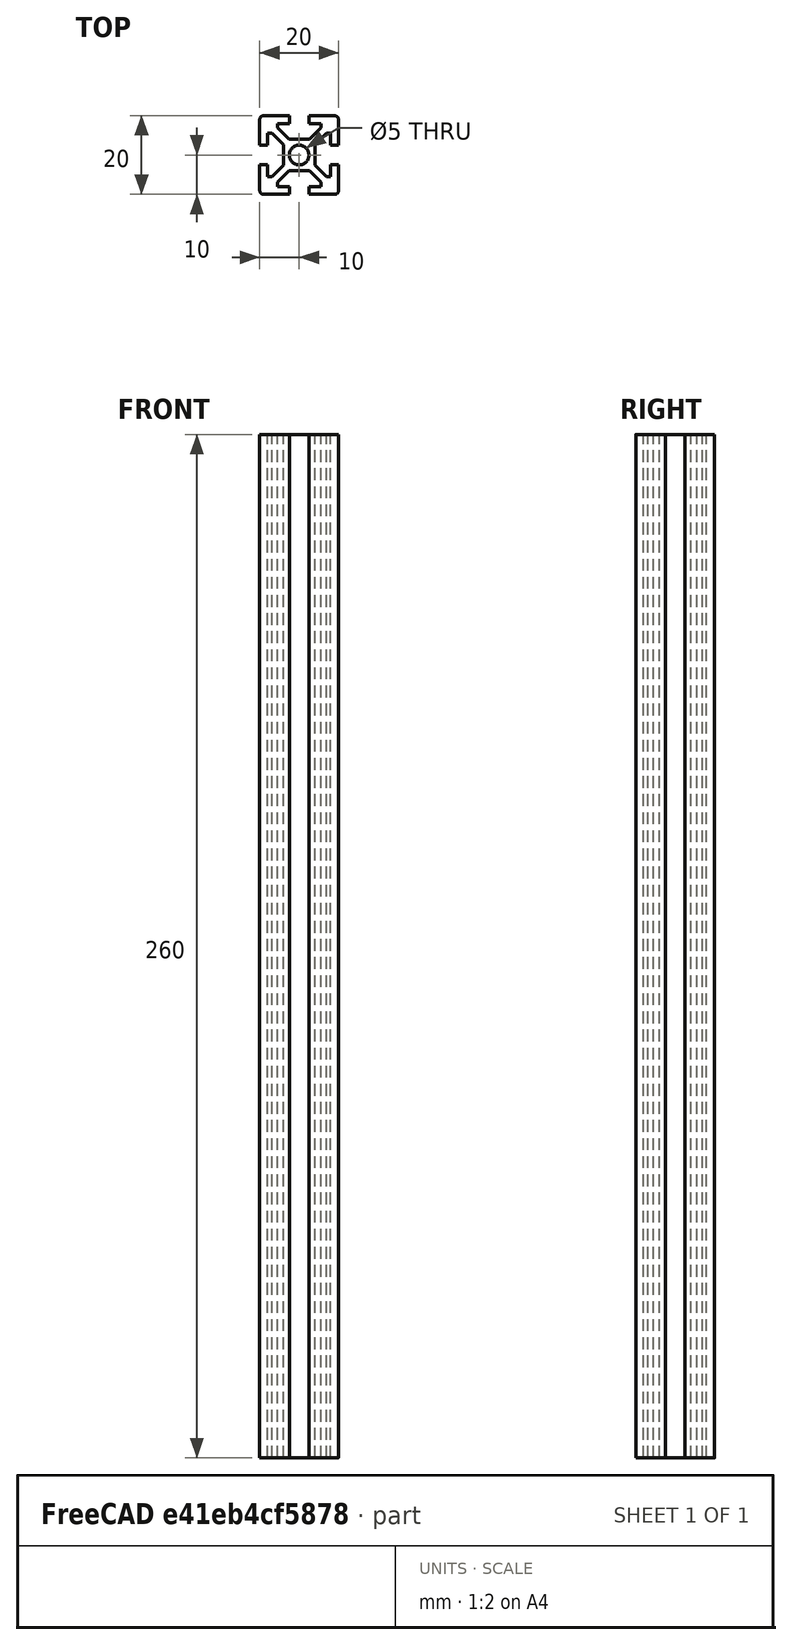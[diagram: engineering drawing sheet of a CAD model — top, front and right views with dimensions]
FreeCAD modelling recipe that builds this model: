
FCSTD DOCUMENT  (FreeCAD 0.18R16117 (Git))
Label: profile2020
License: All rights reserved
LicenseURL: http://en.wikipedia.org/wiki/All_rights_reserved
objects: Sketcher::SketchObject×1, PartDesign::Pad×1, PartDesign::Body×1
note: 4 computed .brp shape members not serialized (recipe doc carries the construction recipe); baked Part::Feature solids carry a one-line shape summary decoded from their .brp

FEATURE [Sketcher::SketchObject] Sketch005  label="profile2020Sketch"
  MapMode = 5
  sketch-geometry (49):
    g0: LineSegment StartX=-4 StartY=-2.58579 StartZ=0 EndX=-4 EndY=2.58579 EndZ=0
    g1: LineSegment StartX=2.58579 StartY=4 StartZ=0 EndX=-2.58579 EndY=4 EndZ=0
    g2: LineSegment StartX=-4 StartY=2.58579 StartZ=0 EndX=-6.91421 EndY=5.5 EndZ=0
    g3: LineSegment StartX=-2.58579 StartY=4 StartZ=0 EndX=-5.5 EndY=6.91421 EndZ=0
    g4: LineSegment StartX=-6.91421 StartY=5.5 StartZ=0 EndX=-8 EndY=5.5 EndZ=0
    g5: LineSegment StartX=-8 StartY=5.5 StartZ=0 EndX=-8 EndY=2.5 EndZ=0
    g6: LineSegment StartX=-5.5 StartY=6.91421 StartZ=0 EndX=-5.5 EndY=8 EndZ=0
    g7: LineSegment StartX=-5.5 StartY=8 StartZ=0 EndX=-2.5 EndY=8 EndZ=0
    g8: LineSegment StartX=-8 StartY=2.5 StartZ=0 EndX=-10 EndY=2.5 EndZ=0
    g9: LineSegment StartX=-2.5 StartY=8 StartZ=0 EndX=-2.5 EndY=10 EndZ=0
    g10: LineSegment StartX=-2.5 StartY=10 StartZ=0 EndX=-9 EndY=10 EndZ=0
    g11: LineSegment StartX=-10 StartY=2.5 StartZ=0 EndX=-10 EndY=9 EndZ=0
    g12: ArcOfCircle CenterX=-9 CenterY=9 CenterZ=0 NormalX=0 NormalY=0 NormalZ=1 AngleXU=0 Radius=1 StartAngle=1.5708 EndAngle=3.14159
    g13: Circle CenterX=0 CenterY=0 CenterZ=0 NormalX=0 NormalY=0 NormalZ=1 AngleXU=0 Radius=2.5
    g14: LineSegment StartX=4 StartY=2.58579 StartZ=0 EndX=4 EndY=-2.58579 EndZ=0
    g15: LineSegment StartX=2.58579 StartY=4 StartZ=0 EndX=5.5 EndY=6.91421 EndZ=0
    g16: LineSegment StartX=5.5 StartY=6.91421 StartZ=0 EndX=5.5 EndY=8 EndZ=0
    g17: LineSegment StartX=5.5 StartY=8 StartZ=0 EndX=2.5 EndY=8 EndZ=0
    g18: LineSegment StartX=2.5 StartY=8 StartZ=0 EndX=2.5 EndY=10 EndZ=0
    g19: LineSegment StartX=4 StartY=2.58579 StartZ=0 EndX=6.91421 EndY=5.5 EndZ=0
    g20: LineSegment StartX=6.91421 StartY=5.5 StartZ=0 EndX=8 EndY=5.5 EndZ=0
    g21: LineSegment StartX=8 StartY=5.5 StartZ=0 EndX=8 EndY=2.5 EndZ=0
    g22: LineSegment StartX=8 StartY=2.5 StartZ=0 EndX=10 EndY=2.5 EndZ=0
    g23: LineSegment StartX=10 StartY=2.5 StartZ=0 EndX=10 EndY=9 EndZ=0
    g24: LineSegment StartX=2.5 StartY=10 StartZ=0 EndX=9 EndY=10 EndZ=0
    g25: ArcOfCircle CenterX=9 CenterY=9 CenterZ=0 NormalX=0 NormalY=0 NormalZ=1 AngleXU=0 Radius=1 StartAngle=5.30563e-07 EndAngle=1.5708
    g26: LineSegment StartX=4 StartY=-2.58579 StartZ=0 EndX=6.91421 EndY=-5.5 EndZ=0
    g27: LineSegment StartX=6.91421 StartY=-5.5 StartZ=0 EndX=8 EndY=-5.5 EndZ=0
    g28: LineSegment StartX=8 StartY=-5.5 StartZ=0 EndX=8 EndY=-2.5 EndZ=0
    g29: LineSegment StartX=8 StartY=-2.5 StartZ=0 EndX=10 EndY=-2.5 EndZ=0
    g30: LineSegment StartX=10 StartY=-2.5 StartZ=0 EndX=10 EndY=-9 EndZ=0
    g31: LineSegment StartX=9 StartY=-10 StartZ=0 EndX=2.5 EndY=-10 EndZ=0
    g32: LineSegment StartX=2.5 StartY=-10 StartZ=0 EndX=2.5 EndY=-8 EndZ=0
    g33: LineSegment StartX=2.5 StartY=-8 StartZ=0 EndX=5.5 EndY=-8 EndZ=0
    g34: LineSegment StartX=5.5 StartY=-8 StartZ=0 EndX=5.5 EndY=-6.91421 EndZ=0
    g35: LineSegment StartX=5.5 StartY=-6.91421 StartZ=0 EndX=2.58579 EndY=-4 EndZ=0
    g36: LineSegment StartX=2.58579 StartY=-4 StartZ=0 EndX=-2.58579 EndY=-4 EndZ=0
    g37: LineSegment StartX=-2.58579 StartY=-4 StartZ=0 EndX=-5.5 EndY=-6.91421 EndZ=0
    g38: LineSegment StartX=-5.5 StartY=-6.91421 StartZ=0 EndX=-5.5 EndY=-8 EndZ=0
    g39: LineSegment StartX=-5.5 StartY=-8 StartZ=0 EndX=-2.5 EndY=-8 EndZ=0
    g40: LineSegment StartX=-2.5 StartY=-8 StartZ=0 EndX=-2.5 EndY=-10 EndZ=0
    g41: LineSegment StartX=-2.5 StartY=-10 StartZ=0 EndX=-9 EndY=-10 EndZ=0
    g42: ArcOfCircle CenterX=9 CenterY=-9 CenterZ=0 NormalX=0 NormalY=0 NormalZ=1 AngleXU=0 Radius=1 StartAngle=4.71239 EndAngle=6.28318
    g43: LineSegment StartX=-4 StartY=-2.58579 StartZ=0 EndX=-6.91421 EndY=-5.5 EndZ=0
    g44: LineSegment StartX=-6.91421 StartY=-5.5 StartZ=0 EndX=-8 EndY=-5.5 EndZ=0
    g45: LineSegment StartX=-8 StartY=-5.5 StartZ=0 EndX=-8 EndY=-2.5 EndZ=0
    g46: LineSegment StartX=-8 StartY=-2.5 StartZ=0 EndX=-10 EndY=-2.5 EndZ=0
    g47: LineSegment StartX=-10 StartY=-2.5 StartZ=0 EndX=-10 EndY=-9 EndZ=0
    g48: ArcOfCircle CenterX=-9 CenterY=-9 CenterZ=0 NormalX=0 NormalY=0 NormalZ=1 AngleXU=0 Radius=1 StartAngle=3.14159 EndAngle=4.71239
  constraints (114):
    c: DistanceX(g-1,g0) = -4
    c: Vertical(g0)
    c: Equal(g0,g1)
    c: Coincident(g0,g2)
    c: Angle(g2,g0) = 2.35619
    c: Coincident(g3,g1)
    c: Parallel(g2,g3)
    c: Equal(g3,g2)
    c: Coincident(g4,g2)
    c: Horizontal(g4)
    c: Coincident(g4,g5)
    c: Vertical(g5)
    c: Coincident(g6,g3)
    c: Vertical(g6)
    c: Equal(g4,g6)
    c: Coincident(g7,g6)
    c: Horizontal(g7)
    c: Equal(g7,g5)
    c: Coincident(g8,g5)
    c: Horizontal(g8)
    c: Coincident(g9,g7)
    c: Vertical(g9)
    c: DistanceX(g-1,g7) = -2.5
    c: DistanceY(g9) = 2
    c: Coincident(g10,g9)
    c: Horizontal(g10)
    c: Coincident(g11,g8)
    c: Vertical(g11)
    c: Equal(g10,g11)
    c: DistanceY(g-1,g10) = 10
    c: Coincident(g12,g11)
    c: Radius(g12) = 1
    c: Tangent(g12,g11)
    c: Equal(g8,g9)
    c: Distance(g1,g0) = 2
    c: DistanceX(g-1,g3) = -5.5
    c: Coincident(g13,g-1)
    c: Radius(g13) = 2.5
    c: DistanceY(g-1,g1) = 4
    c: Symmetric(g14,g0,g-2)
    c: Symmetric(g0,g14,g-2)
    c: Coincident(g15,g1)
    c: Symmetric(g1,g1,g-2)
    c: Symmetric(g15,g3,g-2)
    c: Coincident(g16,g15)
    c: Symmetric(g16,g6,g-2)
    c: Coincident(g17,g16)
    c: Symmetric(g17,g7,g-2)
    c: Coincident(g18,g17)
    c: Symmetric(g18,g9,g-2)
    c: Coincident(g19,g20)
    c: Coincident(g20,g21)
    c: Coincident(g21,g22)
    c: Coincident(g22,g23)
    c: Coincident(g19,g14)
    c: Symmetric(g19,g2,g-2)
    c: Symmetric(g20,g4,g-2)
    c: Symmetric(g21,g5,g-2)
    c: Symmetric(g22,g8,g-2)
    c: Symmetric(g23,g11,g-2)
    c: Coincident(g24,g18)
    c: Symmetric(g24,g10,g-2)
    c: Tangent(g25,g24) = 1.5708
    c: Radius(g25) = 1
    c: Coincident(g25,g23)
    c: Coincident(g26,g27)
    c: Coincident(g27,g28)
    c: Coincident(g28,g29)
    c: Coincident(g29,g30)
    c: Coincident(g26,g14)
    c: Symmetric(g26,g19,g-1)
    c: Symmetric(g27,g20,g-1)
    c: Symmetric(g28,g21,g-1)
    c: Symmetric(g29,g22,g-1)
    c: Symmetric(g30,g23,g-1)
    c: Coincident(g31,g32)
    c: Coincident(g32,g33)
    c: Coincident(g33,g34)
    c: Coincident(g34,g35)
    c: Coincident(g35,g36)
    c: Coincident(g36,g37)
    c: Coincident(g37,g38)
    c: Coincident(g38,g39)
    c: Coincident(g39,g40)
    c: Coincident(g40,g41)
    c: Symmetric(g40,g9,g-1)
    c: Symmetric(g39,g7,g-1)
    c: Symmetric(g38,g6,g-1)
    c: Symmetric(g37,g3,g-1)
    c: Symmetric(g36,g1,g-1)
    c: Symmetric(g35,g1,g-1)
    c: Symmetric(g34,g15,g-1)
    c: Symmetric(g33,g16,g-1)
    c: Symmetric(g32,g17,g-1)
    c: Symmetric(g31,g18,g-1)
    c: Symmetric(g31,g24,g-1)
    c: Radius(g42) = 1
    c: Coincident(g42,g31)
    c: Coincident(g42,g30)
    c: Symmetric(g41,g10,g-1)
    c: Coincident(g43,g44)
    c: Coincident(g44,g45)
    c: Coincident(g45,g46)
    c: Coincident(g46,g47)
    c: Coincident(g0,g43)
    c: Symmetric(g43,g2,g-1)
    c: Symmetric(g44,g4,g-1)
    c: Symmetric(g45,g5,g-1)
    c: Symmetric(g46,g8,g-1)
    c: Symmetric(g47,g11,g-1)
    c: Coincident(g48,g47)
    c: Coincident(g48,g41)
    c: Tangent(g48,g47)
    c: Tangent(g12,g10) = -1.5708
FEATURE [PartDesign::Pad] Pad003
  Length = 260
  Length2 = 100
  Profile = -> Sketch005
  Type = 0
FEATURE [PartDesign::Body] Body003  label="profile2020"
  Group = -> [Sketch005,Pad003]
  Origin = -> Origin003
  Tip = -> Pad003
